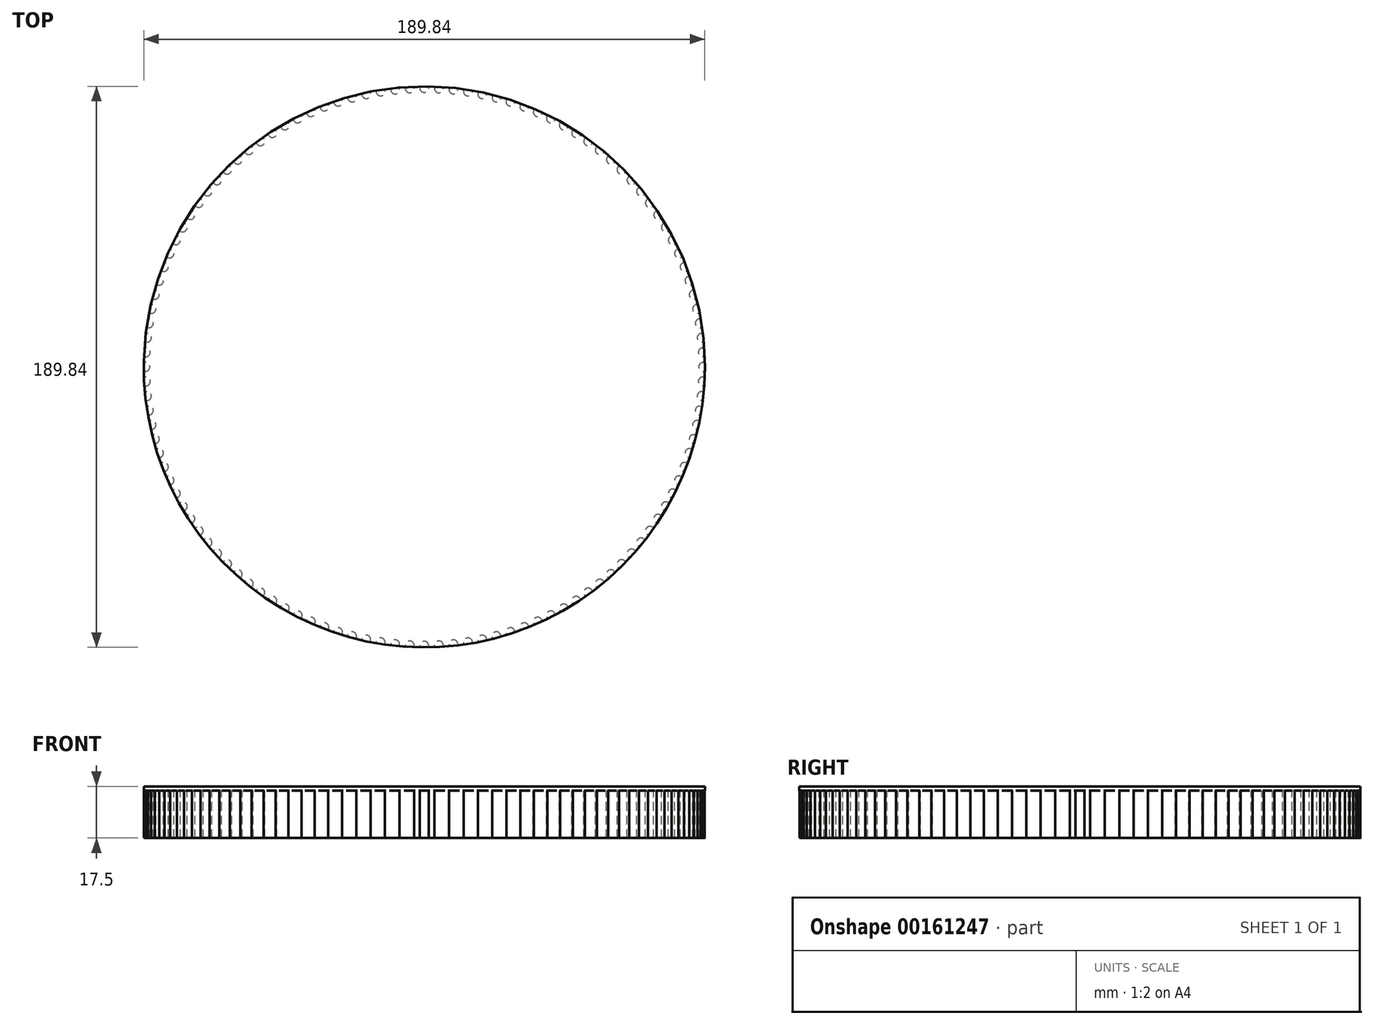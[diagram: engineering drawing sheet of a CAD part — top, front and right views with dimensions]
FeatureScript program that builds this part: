
annotation { "Feature Type Name" : "Feature", "Feature Type Description" : "" }
export const myFeature = defineFeature(function(context is Context, id is Id, definition is map)
    precondition{}
    {
        {
            assignVariable(context, id + "F0", {"name" : "Teeth", "anyValue" : 120});
        }
        {
            assignVariable(context, id + "F1", {"name" : "Width", "anyValue" : 16});
        }
        {
            var Q0;
            Q0=qCreatedBy(makeId("Top.planeOp"),FACE);
            var sketch = newSketch(context, id + "F2", { "sketchPlane" : qUnion([Q0])});
            skCircle(sketch, "E0", {"center": v(0, 0) * mm, "radius": 94.92 * mm});
            skSolve(sketch);
        }
        {
            var Q0;
            Q0=qSketchRegion(id+"F2",true);
            extrude(context, id + "F3", {"entities" : qUnion([Q0]), "flatOperationType" : FlatOperationType.REMOVE, "depth" : (getVariable(context, 'Width')) * mm, "offsetDistance" : 25 * mm, "domain" : OperationDomain.MODEL});
        }
        {
            var Q0;
            Q0=makeQuery(id+"F3.opExtrude","CAP_FACE",FACE,{"disambiguationData":[OSD([sQuery(id+"F2.wireOp",EDGE,"E0")])],"isStart":false});
            var sketch = newSketch(context, id + "F4", { "sketchPlane" : qUnion([Q0])});
            skCircle(sketch, "E1", {"center": v(0, 0) * mm, "radius": 92.86 * mm, "construction": true});
            skArc(sketch, "E2", {"start": v(-1.5, 94.43) * mm, "mid": v(0, 92.86) * mm, "end": v(1.5, 94.43) * mm});
            skArc(sketch, "E3", {"start": v(1.96, 94.9) * mm, "mid": v(0, 94.92) * mm, "end": v(-1.96, 94.9) * mm});
            skArc(sketch, "E4", {"start": v(-1.5, 94.43) * mm, "mid": v(-1.63, 94.76) * mm, "end": v(-1.96, 94.9) * mm});
            skArc(sketch, "E5", {"start": v(1.96, 94.9) * mm, "mid": v(1.63, 94.76) * mm, "end": v(1.5, 94.43) * mm});
            skSolve(sketch);
        }
        {
            var Q0;
            Q0=makeQuery(id+"F4.imprint","IMPRINT",FACE,{"disambiguationData":[TD([[makeQuery(id+"F4.imprint","IMPRINT",EDGE,{"derivedFrom":sQuery(id+"F4.wireOp",EDGE,"E2")}),1.0]])]});
            var Q1;
            Q1=makeQuery(id+"F3.opExtrude","CAP_FACE",FACE,{"disambiguationData":[OSD([sQuery(id+"F2.wireOp",EDGE,"E0")])],"isStart":true});
            extrude(context, id + "F5", {"entities" : qUnion([Q0]), "operationType" : NewBodyOperationType.REMOVE, "endBound" : BoundingType.UP_TO_SURFACE, "oppositeDirection" : true, "endBoundEntityFace" : qUnion([Q1]), "depth" : 25 * mm});
        }
        {
            var Q0;
            Q0=makeQuery(id+"F5.boolean.opBoolean","COPY",FACE,{"derivedFrom":makeQuery(id+"F5.opExtrude","SWEPT_FACE",FACE,{"disambiguationData":[OSD([sQuery(id+"F4.wireOp",EDGE,"E4")])]})});
            var Q1;
            Q1=makeQuery(id+"F5.boolean.opBoolean","COPY",FACE,{"derivedFrom":makeQuery(id+"F5.opExtrude","SWEPT_FACE",FACE,{"disambiguationData":[OSD([sQuery(id+"F4.wireOp",EDGE,"kHu0Iwj9-o4Cv-DRlk-4OjM-lw9Y4UkXsprA")])]})});
            var Q2;
            Q2=makeQuery(id+"F5.boolean.opBoolean","COPY",FACE,{"derivedFrom":makeQuery(id+"F5.opExtrude","SWEPT_FACE",FACE,{"disambiguationData":[OSD([sQuery(id+"F4.wireOp",EDGE,"E2")])]})});
            var Q3;
            Q3=makeQuery(id+"F5.boolean.opBoolean","COPY",FACE,{"derivedFrom":makeQuery(id+"F5.opExtrude","SWEPT_FACE",FACE,{"disambiguationData":[OSD([sQuery(id+"F4.wireOp",EDGE,"lCBZwTSR-BtAH-iuKv-YoZ4-wjcx4KIexOll")])]})});
            var Q4;
            Q4=makeQuery(id+"F5.boolean.opBoolean","COPY",FACE,{"derivedFrom":makeQuery(id+"F5.opExtrude","SWEPT_FACE",FACE,{"disambiguationData":[OSD([sQuery(id+"F4.wireOp",EDGE,"E5")])]})});
            var Q5;
            Q5=makeQuery(id+"F3.opExtrude","SWEPT_FACE",FACE,{"disambiguationData":[OSD([sQuery(id+"F2.wireOp",EDGE,"E0")])]});
            circularPattern(context, id + "F6", {"faces" : qUnion([Q0, Q1, Q2, Q3, Q4]), "axis" : qUnion([Q5]), "angle" : 360 * degree, "instanceCount" : getVariable(context, 'Teeth'), "equalSpace" : true, "patternType" : PatternType.FACE, "computeTransformsWithoutBuiltin" : true});
        }
        {
            var Q0;
            Q0=makeQuery(id+"F3.opExtrude","CAP_FACE",FACE,{"disambiguationData":[OSD([sQuery(id+"F2.wireOp",EDGE,"E0")])],"isStart":false});
            var sketch = newSketch(context, id + "F7", { "sketchPlane" : qUnion([Q0])});
            skCircle(sketch, "E6.0", {"center": v(0, 0) * mm, "radius": 94.92 * mm});
            skSolve(sketch);
        }
        {
            var Q0;
            Q0=qSketchRegion(id+"F7",true);
            extrude(context, id + "F8", {"entities" : qUnion([Q0]), "operationType" : NewBodyOperationType.ADD, "depth" : 1.5 * mm});
        }
    });
